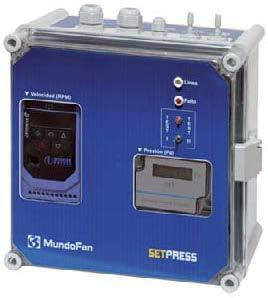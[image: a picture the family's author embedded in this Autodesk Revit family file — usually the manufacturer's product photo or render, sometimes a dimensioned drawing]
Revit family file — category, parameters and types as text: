
# Revit family: SETPRESS-22_VE10810
name_source: partatom
category: Aparatos eléctricos
revit_build: Autodesk Revit 2016 (Build: 20150220_1215(x64)
units: mm (PartAtom-declared; Revit-internal decimal feet)

## family parameters
Compartido = No
Corte con vacíos al cargar = No
Cota de conector redondo = Diámetro de uso
Mantener orientación de anotación = No
Número OmniClass = 23.80.00.00
Punto de cálculo de habitación = No
Se basa en plano de trabajo = No
Siempre vertical = Sí
Tipo de pieza = Caja de conexiones
Título OmniClass = Electric Power and Lighting

## types (1)
- SETPRESS
    Alimentación = 400Vac trifásico
    Corriente = 5,8 A
    Costo = 0 $
    Código de montaje = VE10810
    Descripción = CONTROL EFICIENCIA ENERGETICA PARA VENTILADORES
    Dimensiones máx. = 270x300x170 mm
    Fabricante = SALVADOR ESCODA
    Imagen de tipo = setpress.jpg
    Leds = linea / fallo
    Modelo = SETPRESS 2,2 kW
    Normativas = UNE-EN 12101-6
    Potencia = 2,2 kW
    Regulación = Mediante sonda analógica de presión
    Salida = 400Vac trifásico
    URL = www.salvadorescoda.com
    Visualización = frecuencia (Hz) y presión (Pa)
